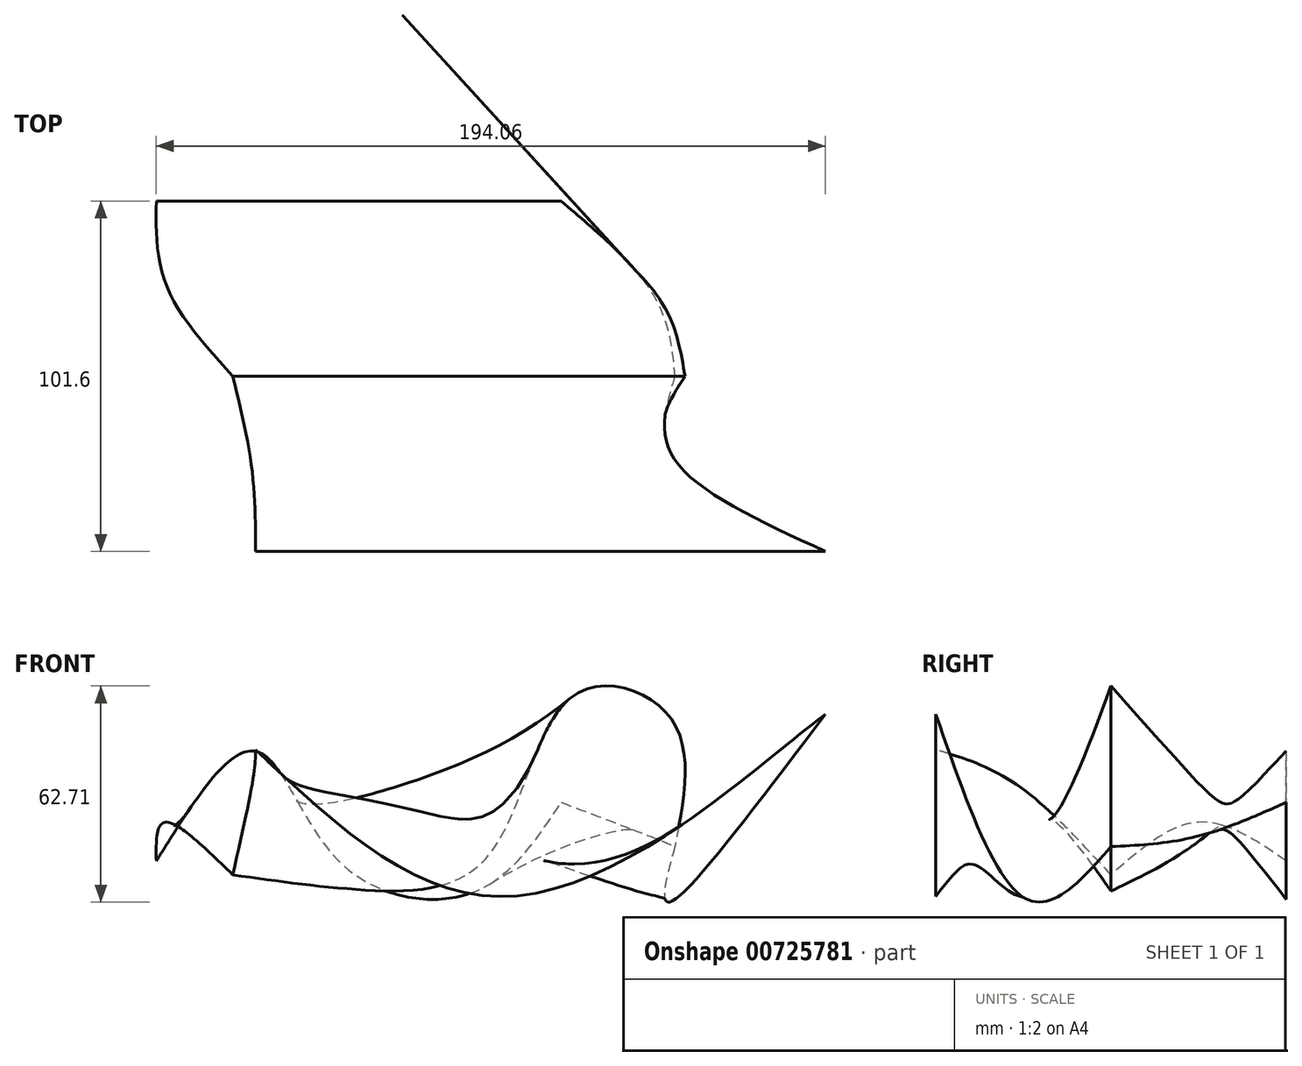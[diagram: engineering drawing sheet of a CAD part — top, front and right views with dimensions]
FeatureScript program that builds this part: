
annotation { "Feature Type Name" : "Feature", "Feature Type Description" : "" }
export const myFeature = defineFeature(function(context is Context, id is Id, definition is map)
    precondition{}
    {
        {
            var Q0;
            Q0=qCreatedBy(makeId("Front.planeOp"),FACE);
            cPlane(context, id + "F0", {"entities" : qUnion([Q0]), "cplaneType" : CPlaneType.OFFSET, "offset" : 25.4 * mm, "width" : 152.4 * mm, "height" : 152.4 * mm});
        }
        {
            var Q0;
            Q0=qCreatedBy(id+"F0.planeOp",FACE);
            cPlane(context, id + "F1", {"entities" : qUnion([Q0]), "cplaneType" : CPlaneType.OFFSET, "offset" : 25.4 * mm, "width" : 152.4 * mm, "height" : 152.4 * mm});
        }
        {
            var Q0;
            Q0=qCreatedBy(id+"F1.planeOp",FACE);
            cPlane(context, id + "F2", {"entities" : qUnion([Q0]), "cplaneType" : CPlaneType.OFFSET, "offset" : 25.4 * mm, "width" : 152.4 * mm, "height" : 152.4 * mm});
        }
        {
            var Q0;
            Q0=qCreatedBy(id+"F2.planeOp",FACE);
            cPlane(context, id + "F3", {"entities" : qUnion([Q0]), "cplaneType" : CPlaneType.OFFSET, "offset" : 25.4 * mm, "width" : 152.4 * mm, "height" : 152.4 * mm});
        }
        {
            var Q0;
            Q0=qCreatedBy(makeId("Front.planeOp"),FACE);
            var sketch = newSketch(context, id + "F4", { "sketchPlane" : qUnion([Q0])});
            skFitSpline(sketch, "E0", {"points": [v(-72.54, -17.03) * mm, v(-43.6, 14.8) * mm, v(-19.89, -16.72) * mm, v(19.09, -26.16) * mm, v(44.87, 0) * mm], "startDerivative": vector(120.94, 194.28) * mm, "endDerivative": vector(90.27, 136.83) * mm});
            skSolve(sketch);
        }
        {
            var Q0;
            Q0=qCreatedBy(id+"F1.planeOp",FACE);
            var sketch = newSketch(context, id + "F5", { "sketchPlane" : qUnion([Q0])});
            skFitSpline(sketch, "E1", {"points": [v(-50.36, -21.02) * mm, v(-13.45, -25.34) * mm, v(23.23, -16.08) * mm, v(48.7, 31.13) * mm, v(76.57, 24.49) * mm, v(77.81, -12.86) * mm], "startDerivative": vector(181.77, -26.04) * mm, "endDerivative": vector(-42.31, -214.16) * mm});
            skSolve(sketch);
        }
        {
            var Q0;
            Q0=qCreatedBy(id+"F0.planeOp",FACE);
            var sketch = newSketch(context, id + "F6", { "sketchPlane" : qUnion([Q0])});
            skFitSpline(sketch, "E2", {"points": [v(-69.22, -5.76) * mm, v(-45.36, -11) * mm, v(0, 4.58) * mm, v(70.37, -5.5) * mm, v(70.46, -9.77) * mm], "startDerivative": vector(105.84, -44.37) * mm, "endDerivative": vector(-20.63, -45.17) * mm});
            skSolve(sketch);
        }
        {
            var Q0;
            Q0=qCreatedBy(id+"F2.planeOp",FACE);
            var sketch = newSketch(context, id + "F7", { "sketchPlane" : qUnion([Q0])});
            skFitSpline(sketch, "E3", {"points": [v(-45.02, 3.75) * mm, v(12.04, -4.86) * mm, v(70.25, -26.65) * mm, v(78.66, -27.54) * mm], "startDerivative": vector(130.61, -8.27) * mm, "endDerivative": vector(41.03, 2.28) * mm});
            skSolve(sketch);
        }
        {
            var Q0;
            Q0=qCreatedBy(id+"F3.planeOp",FACE);
            var sketch = newSketch(context, id + "F8", { "sketchPlane" : qUnion([Q0])});
            skFitSpline(sketch, "E4", {"points": [v(-43.76, 15.29) * mm, v(31.68, -27.15) * mm, v(108, 14.92) * mm, v(121.48, 25.61) * mm], "startDerivative": vector(173.73, -164.56) * mm, "endDerivative": vector(55.11, 42.6) * mm});
            skSolve(sketch);
        }
        {
            var Q0;
            Q0=sQuery(id+"F4.wireOp",EDGE,"E0");
            var Q1;
            Q1=sQuery(id+"F6.wireOp",EDGE,"E2");
            var Q2;
            Q2=sQuery(id+"F5.wireOp",EDGE,"E1");
            loft(context, id + "F9", {"bodyType" : ToolBodyType.SURFACE, "wireProfilesArray" : [{ "wireProfileEntities" : qUnion([Q0]) }, { "wireProfileEntities" : qUnion([Q1]) }, { "wireProfileEntities" : qUnion([Q2]) }]});
        }
        {
            var Q0;
            Q0=makeQuery(id+"F9.opLoft","MID_CAP_EDGE",EDGE,{"disambiguationData":[OSD([sQuery(id+"F5.wireOp",VERTEX,"E1.start"),sQuery(id+"F5.wireOp",VERTEX,"E1.end"),sQuery(id+"F5.wireOp",EDGE,"E1")])],"capPos":2.0});
            var Q1;
            Q1=sQuery(id+"F7.wireOp",EDGE,"E3");
            var Q2;
            Q2=sQuery(id+"F8.wireOp",EDGE,"E4");
            loft(context, id + "F10", {"bodyType" : ToolBodyType.SURFACE, "surfaceOperationType" : NewSurfaceOperationType.ADD, "wireProfilesArray" : [{ "wireProfileEntities" : qUnion([Q0]) }, { "wireProfileEntities" : qUnion([Q1]) }, { "wireProfileEntities" : qUnion([Q2]) }]});
        }
    });
